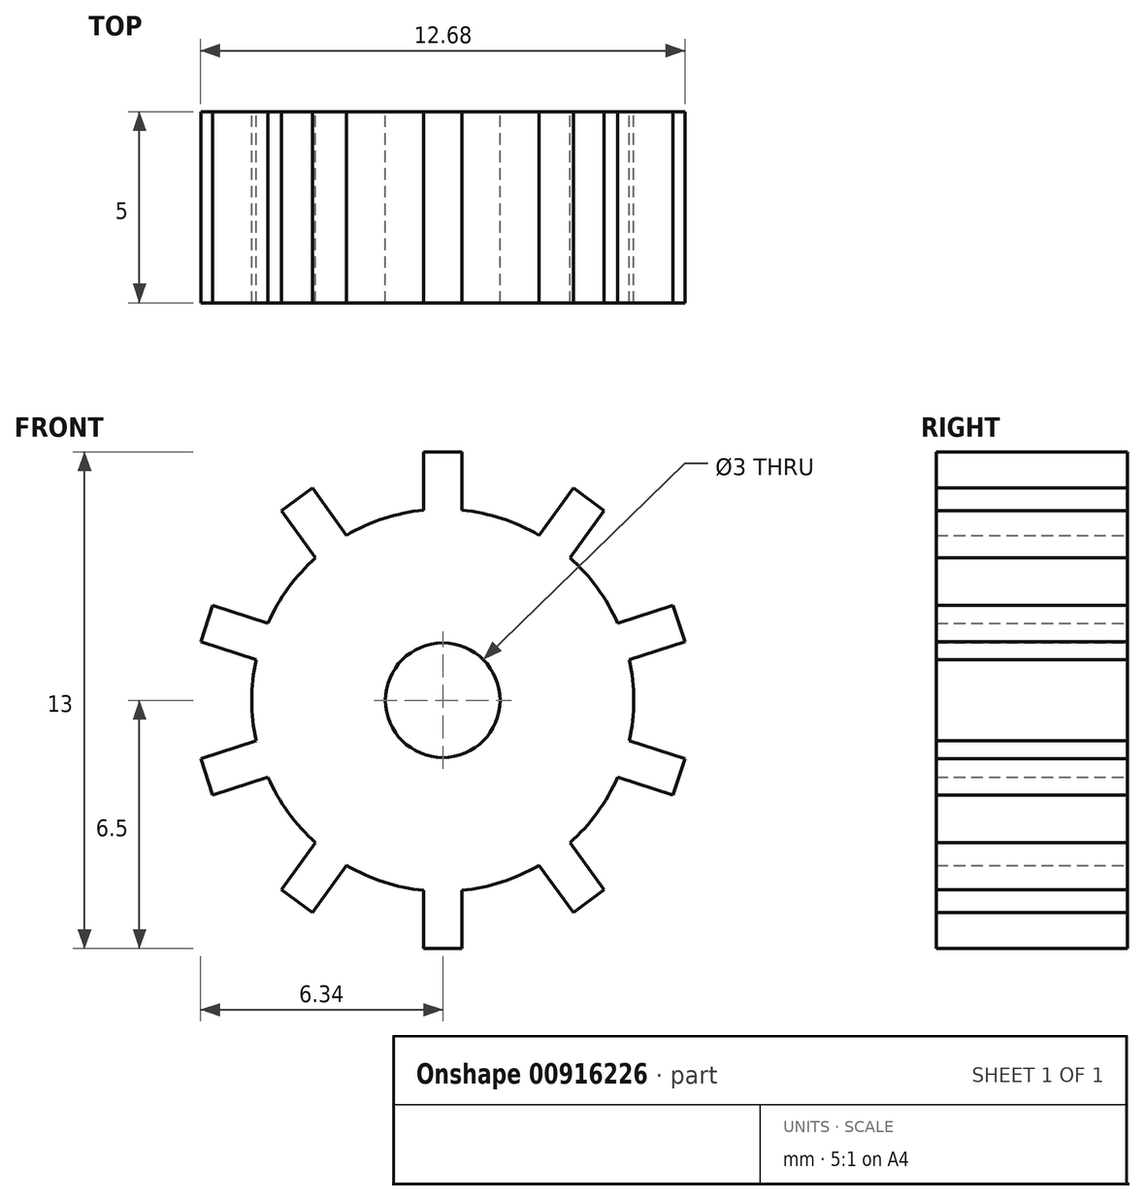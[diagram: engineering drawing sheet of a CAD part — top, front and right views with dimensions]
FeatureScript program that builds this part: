
annotation { "Feature Type Name" : "Feature", "Feature Type Description" : "" }
export const myFeature = defineFeature(function(context is Context, id is Id, definition is map)
    precondition{}
    {
        {
            var Q0;
            Q0=qCreatedBy(makeId("Front.planeOp"),FACE);
            var sketch = newSketch(context, id + "F0", { "sketchPlane" : qUnion([Q0])});
            skCircle(sketch, "E0", {"center": v(0, 0) * mm, "radius": 1.5 * mm});
            skCircle(sketch, "E1", {"center": v(0, 0) * mm, "radius": 5 * mm});
            skLineSegment(sketch, "E2", {"start": v(-0.5, 6.5) * mm, "end": v(0.5, 6.5) * mm});
            skLineSegment(sketch, "E3", {"start": v(0.5, 6.5) * mm, "end": v(0.5, 4.97) * mm});
            skLineSegment(sketch, "E4.MirrorCS", {"start": v(-0.5, 6.5) * mm, "end": v(-0.5, 4.97) * mm});
            skLineSegment(sketch, "E5.1.0", {"start": v(-3.42, 5.55) * mm, "end": v(-2.52, 4.32) * mm});
            skLineSegment(sketch, "E5.1.1", {"start": v(-4.23, 4.96) * mm, "end": v(-3.42, 5.55) * mm});
            skLineSegment(sketch, "E5.1.2", {"start": v(-4.23, 4.96) * mm, "end": v(-3.33, 3.73) * mm});
            skLineSegment(sketch, "E5.2.0", {"start": v(-6.03, 2.48) * mm, "end": v(-4.58, 2.01) * mm});
            skLineSegment(sketch, "E5.2.1", {"start": v(-6.34, 1.53) * mm, "end": v(-6.03, 2.48) * mm});
            skLineSegment(sketch, "E5.2.2", {"start": v(-6.34, 1.53) * mm, "end": v(-4.89, 1.06) * mm});
            skLineSegment(sketch, "E6.2.3.0", {"start": v(-6.34, -1.53) * mm, "end": v(-4.89, -1.06) * mm});
            skLineSegment(sketch, "E6.3.3.0", {"start": v(-6.03, -2.48) * mm, "end": v(-6.34, -1.53) * mm});
            skLineSegment(sketch, "E6.6.3.0", {"start": v(-6.03, -2.48) * mm, "end": v(-4.58, -2.01) * mm});
            skLineSegment(sketch, "E6.2.4.0", {"start": v(-4.23, -4.96) * mm, "end": v(-3.33, -3.73) * mm});
            skLineSegment(sketch, "E6.3.4.0", {"start": v(-3.42, -5.55) * mm, "end": v(-4.23, -4.96) * mm});
            skLineSegment(sketch, "E6.6.4.0", {"start": v(-3.42, -5.55) * mm, "end": v(-2.52, -4.32) * mm});
            skLineSegment(sketch, "E6.2.5.0", {"start": v(-0.5, -6.5) * mm, "end": v(-0.5, -4.97) * mm});
            skLineSegment(sketch, "E6.3.5.0", {"start": v(0.5, -6.5) * mm, "end": v(-0.5, -6.5) * mm});
            skLineSegment(sketch, "E6.6.5.0", {"start": v(0.5, -6.5) * mm, "end": v(0.5, -4.97) * mm});
            skLineSegment(sketch, "E6.2.6.0", {"start": v(3.42, -5.55) * mm, "end": v(2.52, -4.32) * mm});
            skLineSegment(sketch, "E6.3.6.0", {"start": v(4.23, -4.96) * mm, "end": v(3.42, -5.55) * mm});
            skLineSegment(sketch, "E6.6.6.0", {"start": v(4.23, -4.96) * mm, "end": v(3.33, -3.73) * mm});
            skLineSegment(sketch, "E6.2.7.0", {"start": v(6.03, -2.48) * mm, "end": v(4.58, -2.01) * mm});
            skLineSegment(sketch, "E6.3.7.0", {"start": v(6.34, -1.53) * mm, "end": v(6.03, -2.48) * mm});
            skLineSegment(sketch, "E6.6.7.0", {"start": v(6.34, -1.53) * mm, "end": v(4.89, -1.06) * mm});
            skLineSegment(sketch, "E6.2.8.0", {"start": v(6.34, 1.53) * mm, "end": v(4.89, 1.06) * mm});
            skLineSegment(sketch, "E6.3.8.0", {"start": v(6.03, 2.48) * mm, "end": v(6.34, 1.53) * mm});
            skLineSegment(sketch, "E6.6.8.0", {"start": v(6.03, 2.48) * mm, "end": v(4.58, 2.01) * mm});
            skLineSegment(sketch, "E6.2.9.0", {"start": v(4.23, 4.96) * mm, "end": v(3.33, 3.73) * mm});
            skLineSegment(sketch, "E6.3.9.0", {"start": v(3.42, 5.55) * mm, "end": v(4.23, 4.96) * mm});
            skLineSegment(sketch, "E6.6.9.0", {"start": v(3.42, 5.55) * mm, "end": v(2.52, 4.32) * mm});
            skSolve(sketch);
        }
        {
            var Q0;
            Q0 = qSketchRegion(id + "F0", true);
            extrude(context, id + "F1", {"entities" : qUnion([Q0]), "depth" : 5 * mm, "offsetDistance" : 25 * mm});
        }
    });
